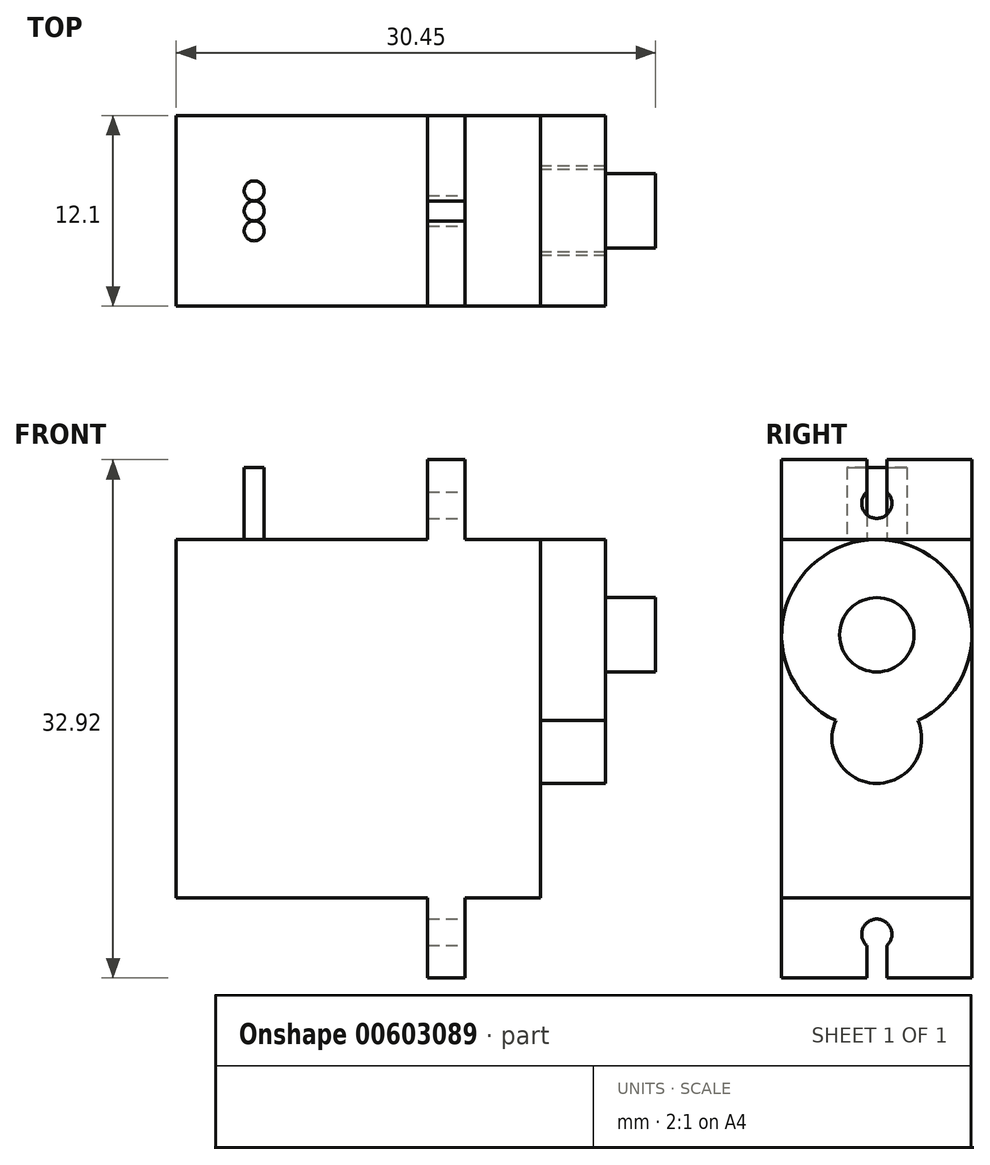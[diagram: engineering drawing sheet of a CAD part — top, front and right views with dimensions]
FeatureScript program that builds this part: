
annotation { "Feature Type Name" : "Feature", "Feature Type Description" : "" }
export const myFeature = defineFeature(function(context is Context, id is Id, definition is map)
    precondition{}
    {
        {
            var Q0;
            Q0=qCreatedBy(makeId("Front.planeOp"),FACE);
            var sketch = newSketch(context, id + "F0", { "sketchPlane" : qUnion([Q0])});
            skLineSegment(sketch, "E0.bottom", {"start": v(11.57, -11.38) * mm, "end": v(-11.57, -11.38) * mm});
            skLineSegment(sketch, "E0.top", {"start": v(11.57, 11.38) * mm, "end": v(-11.57, 11.38) * mm});
            skLineSegment(sketch, "E0.left", {"start": v(11.57, -11.38) * mm, "end": v(11.57, 11.38) * mm});
            skLineSegment(sketch, "E0.right", {"start": v(-11.57, -11.38) * mm, "end": v(-11.57, 11.38) * mm});
            skPoint(sketch, "E0.middle", {"position": v(0, 0) * mm});
            skLineSegment(sketch, "E1.bottom", {"start": v(4.4, 11.38) * mm, "end": v(6.77, 11.38) * mm});
            skLineSegment(sketch, "E1.top", {"start": v(4.4, 16.46) * mm, "end": v(6.77, 16.46) * mm});
            skLineSegment(sketch, "E1.left", {"start": v(4.4, 11.38) * mm, "end": v(4.4, 16.46) * mm});
            skLineSegment(sketch, "E1.right", {"start": v(6.77, 11.38) * mm, "end": v(6.77, 16.46) * mm});
            skLineSegment(sketch, "E2.bottom", {"start": v(4.4, -11.38) * mm, "end": v(6.77, -11.38) * mm});
            skLineSegment(sketch, "E2.top", {"start": v(4.4, -16.46) * mm, "end": v(6.77, -16.46) * mm});
            skLineSegment(sketch, "E2.left", {"start": v(4.4, -11.38) * mm, "end": v(4.4, -16.46) * mm});
            skLineSegment(sketch, "E2.right", {"start": v(6.77, -11.38) * mm, "end": v(6.77, -16.46) * mm});
            skSolve(sketch);
        }
        {
            var Q0;
            Q0 = qSketchRegion(id + "F0", true);
            extrude(context, id + "F1", {"entities" : qUnion([Q0]), "endBound" : BoundingType.SYMMETRIC, "depth" : 12.1 * mm, "offsetDistance" : 25.4 * mm});
        }
        {
            var Q0;
            Q0=makeQuery(id+"F1.opExtrude","SWEPT_FACE",FACE,{"disambiguationData":[OSD([sQuery(id+"F0.wireOp",EDGE,"E0.left")])]});
            var sketch = newSketch(context, id + "F2", { "sketchPlane" : qUnion([Q0])});
            skCircle(sketch, "E3", {"center": v(0, 5.33) * mm, "radius": 6.05 * mm});
            skCircle(sketch, "E4", {"center": v(0, -1.26) * mm, "radius": 2.84 * mm});
            skSolve(sketch);
        }
        {
            var Q0;
            Q0 = qSketchRegion(id + "F2", true);
            extrude(context, id + "F3", {"entities" : qUnion([Q0]), "operationType" : NewBodyOperationType.ADD, "depth" : 4.14 * mm, "offsetDistance" : 25.4 * mm});
        }
        {
            var Q0;
            Q0=makeQuery(id+"F3.opExtrude","CAP_FACE",FACE,{"disambiguationData":[OSD([sQuery(id+"F2.wireOp",EDGE,"E3")])],"isStart":false});
            var sketch = newSketch(context, id + "F4", { "sketchPlane" : qUnion([Q0])});
            skCircle(sketch, "E5", {"center": v(0, 5.33) * mm, "radius": 2.36 * mm});
            skSolve(sketch);
        }
        {
            var Q0;
            Q0 = qSketchRegion(id + "F4", true);
            extrude(context, id + "F5", {"entities" : qUnion([Q0]), "operationType" : NewBodyOperationType.ADD, "depth" : 3.17 * mm, "offsetDistance" : 25.4 * mm});
        }
        {
            var Q0;
            Q0=makeQuery(id+"F1.opExtrude","SWEPT_FACE",FACE,{"disambiguationData":[OSD([sQuery(id+"F0.wireOp",EDGE,"E1.right")])]});
            var sketch = newSketch(context, id + "F6", { "sketchPlane" : qUnion([Q0])});
            skLineSegment(sketch, "E6.bottom", {"start": v(0.64, 16.46) * mm, "end": v(-0.63, 16.46) * mm});
            skLineSegment(sketch, "E6.top", {"start": v(0.63, 13.68) * mm, "end": v(-0.63, 13.68) * mm});
            skLineSegment(sketch, "E6.left", {"start": v(0.64, 16.46) * mm, "end": v(0.64, 13.68) * mm});
            skLineSegment(sketch, "E6.right", {"start": v(-0.63, 16.46) * mm, "end": v(-0.63, 13.68) * mm});
            skPoint(sketch, "E6.middle", {"position": v(0, 15.07) * mm});
            skPoint(sketch, "E6.middle.positionSnap0", {"position": v(0, 16.46) * mm});
            skPoint(sketch, "E6.centerSnap0", {"position": v(0, 16.46) * mm});
            skCircle(sketch, "E7", {"center": v(0, 13.68) * mm, "radius": 0.96 * mm});
            skPoint(sketch, "E8.MirrorP", {"position": v(0, -16.46) * mm});
            skPoint(sketch, "E9.MirrorP", {"position": v(0, -15.07) * mm});
            skLineSegment(sketch, "E10.MirrorCS", {"start": v(0.63, -13.68) * mm, "end": v(-0.63, -13.68) * mm});
            skLineSegment(sketch, "E11.MirrorCS", {"start": v(0.64, -16.46) * mm, "end": v(0.64, -13.68) * mm});
            skLineSegment(sketch, "E12.MirrorCS", {"start": v(0.64, -16.46) * mm, "end": v(-0.63, -16.46) * mm});
            skLineSegment(sketch, "E13.MirrorCS", {"start": v(-0.63, -16.46) * mm, "end": v(-0.63, -13.68) * mm});
            skCircle(sketch, "E14.MirrorC", {"center": v(0, -13.68) * mm, "radius": 0.96 * mm});
            skSolve(sketch);
        }
        {
            var Q0;
            Q0 = qSketchRegion(id + "F6", true);
            extrude(context, id + "F7", {"entities" : qUnion([Q0]), "operationType" : NewBodyOperationType.REMOVE, "oppositeDirection" : true, "depth" : 25.4 * mm, "offsetDistance" : 25.4 * mm});
        }
        {
            var Q0;
            {var subQ0=sQuery(id+"F0.wireOp",EDGE,"E0.top");Q0=makeQuery(id+"F1.opExtrude","SWEPT_FACE",FACE,{"disambiguationData":[OSD([subQ0]),TDD([makeQuery(id+"F0.imprint","IMPRINT",EDGE,{"disambiguationData":[TD([[makeQuery(id+"F0.imprint","INTERSECT",VERTEX,{"derivedFrom":[subQ0,sQuery(id+"F0.wireOp",EDGE,"E0.right")]}),1.0]])],"derivedFrom":subQ0})])]});}
            var sketch = newSketch(context, id + "F8", { "sketchPlane" : qUnion([Q0])});
            skCircle(sketch, "E15", {"center": v(-6.62, 0) * mm, "radius": 0.64 * mm});
            skCircle(sketch, "E16", {"center": v(-6.62, 1.27) * mm, "radius": 0.64 * mm});
            skCircle(sketch, "E17", {"center": v(-6.62, -1.27) * mm, "radius": 0.64 * mm});
            skSolve(sketch);
        }
        {
            var Q0;
            Q0 = qSketchRegion(id + "F8", true);
            extrude(context, id + "F9", {"entities" : qUnion([Q0]), "depth" : 4.57 * mm, "offsetDistance" : 25.4 * mm});
        }
    });
